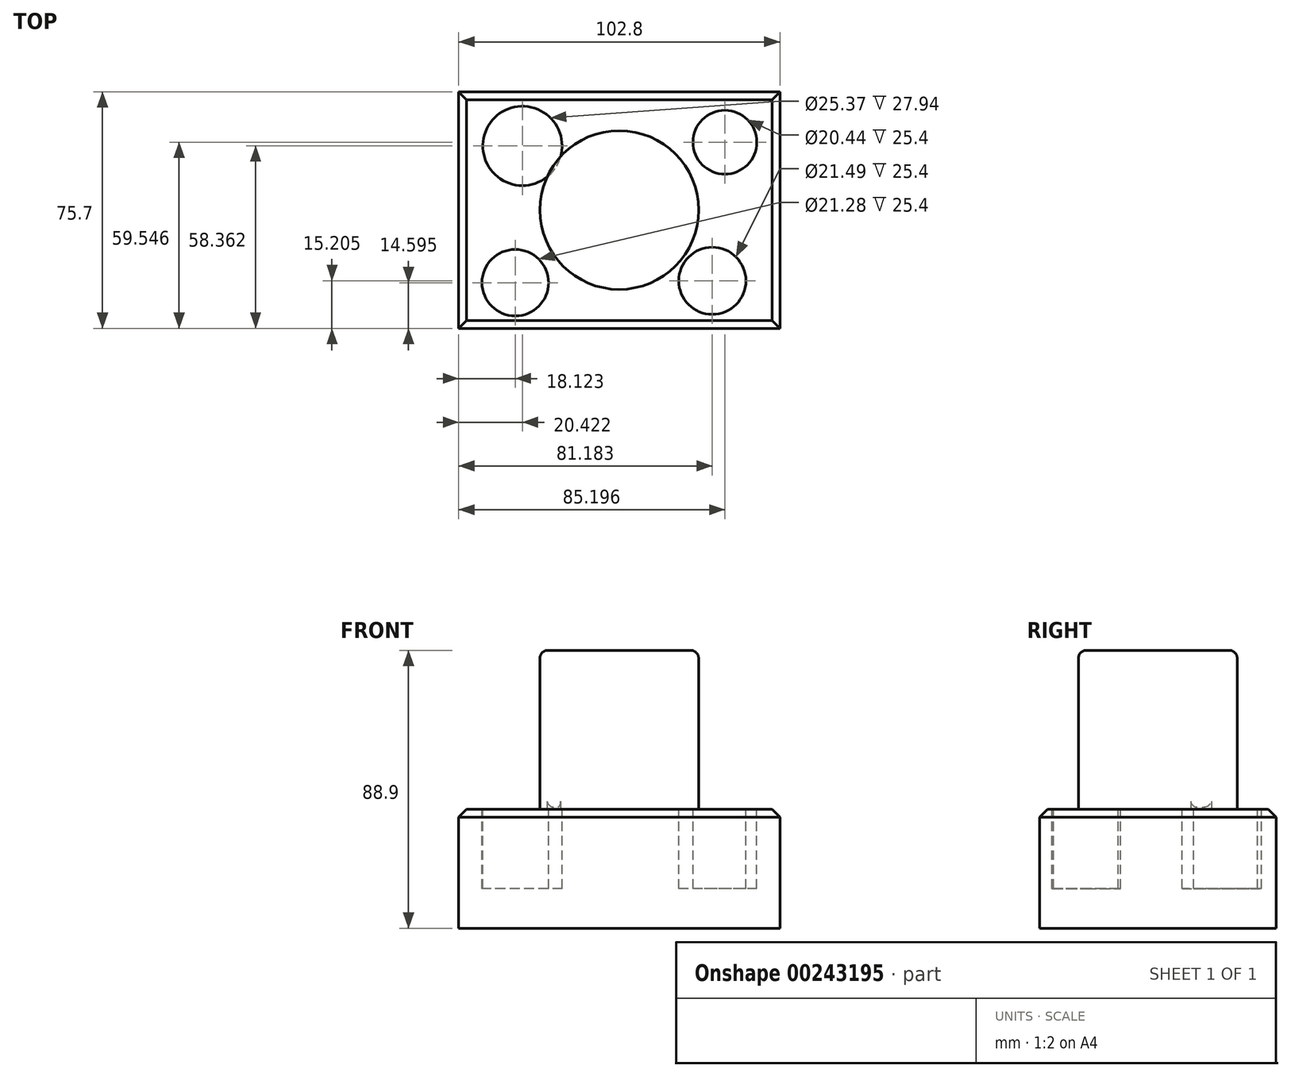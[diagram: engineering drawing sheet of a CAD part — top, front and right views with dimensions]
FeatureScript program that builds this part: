
annotation { "Feature Type Name" : "Feature", "Feature Type Description" : "" }
export const myFeature = defineFeature(function(context is Context, id is Id, definition is map)
    precondition{}
    {
        {
            var Q0;
            Q0=qCreatedBy(makeId("Top.planeOp"),FACE);
            var sketch = newSketch(context, id + "F0", { "sketchPlane" : qUnion([Q0])});
            skLineSegment(sketch, "E0.bottom", {"start": v(-51.4, 37.85) * mm, "end": v(51.4, 37.85) * mm});
            skLineSegment(sketch, "E0.top", {"start": v(-51.4, -37.85) * mm, "end": v(51.4, -37.85) * mm});
            skLineSegment(sketch, "E0.left", {"start": v(-51.4, 37.85) * mm, "end": v(-51.4, -37.85) * mm});
            skLineSegment(sketch, "E0.right", {"start": v(51.4, 37.85) * mm, "end": v(51.4, -37.85) * mm});
            skPoint(sketch, "E0.middle", {"position": v(0, 0) * mm});
            skSolve(sketch);
        }
        {
            var Q0;
            Q0=makeQuery(id+"F0.imprint","IMPRINT",FACE,{"disambiguationData":[TD([[makeQuery(id+"F0.imprint","IMPRINT",EDGE,{"derivedFrom":sQuery(id+"F0.wireOp",EDGE,"E0.bottom")}),-1.0]])]});
            extrude(context, id + "F1", {"entities" : qUnion([Q0]), "depth" : 38.1 * mm});
        }
        {
            var Q0;
            Q0=makeQuery(id+"F1.opExtrude","CAP_FACE",FACE,{"disambiguationData":[OSD([sQuery(id+"F0.wireOp",EDGE,"E0.bottom"),sQuery(id+"F0.wireOp",EDGE,"E0.top"),sQuery(id+"F0.wireOp",EDGE,"E0.left"),sQuery(id+"F0.wireOp",EDGE,"E0.right")])],"isStart":false});
            var sketch = newSketch(context, id + "F2", { "sketchPlane" : qUnion([Q0])});
            skLineSegment(sketch, "E1.0.1", {"start": v(-51.4, -37.85) * mm, "end": v(51.4, -37.85) * mm});
            skLineSegment(sketch, "E1.0.3", {"start": v(51.4, 37.85) * mm, "end": v(-51.4, 37.85) * mm});
            skCircle(sketch, "E2", {"center": v(-30.98, 20.51) * mm, "radius": 12.68 * mm});
            skPoint(sketch, "E2.first.point", {"position": v(-38.59, 10.36) * mm});
            skPoint(sketch, "E2.second.point", {"position": v(-21.36, 28.78) * mm});
            skPoint(sketch, "E2.third.point", {"position": v(-23.1, 10.57) * mm});
            skCircle(sketch, "E3", {"center": v(33.8, 21.7) * mm, "radius": 10.22 * mm});
            skPoint(sketch, "E3.first.point", {"position": v(39.42, 30.23) * mm});
            skPoint(sketch, "E3.second.point", {"position": v(23.63, 20.64) * mm});
            skPoint(sketch, "E3.third.point", {"position": v(41.09, 14.54) * mm});
            skCircle(sketch, "E4", {"center": v(-33.28, -23.25) * mm, "radius": 10.64 * mm});
            skCircle(sketch, "E5", {"center": v(29.78, -22.64) * mm, "radius": 10.74 * mm});
            skSolve(sketch);
        }
        {
            var Q0;
            Q0=makeQuery(id+"F2.imprint","IMPRINT",FACE,{"disambiguationData":[TD([[makeQuery(id+"F2.imprint","IMPRINT",EDGE,{"derivedFrom":sQuery(id+"F2.wireOp",EDGE,"E2")}),1.0]])]});
            var Q1;
            Q1=makeQuery(id+"F2.imprint","IMPRINT",FACE,{"disambiguationData":[TD([[makeQuery(id+"F2.imprint","IMPRINT",EDGE,{"derivedFrom":sQuery(id+"F2.wireOp",EDGE,"E3")}),1.0]])]});
            var Q2;
            Q2=makeQuery(id+"F2.imprint","IMPRINT",FACE,{"disambiguationData":[TD([[makeQuery(id+"F2.imprint","IMPRINT",EDGE,{"derivedFrom":sQuery(id+"F2.wireOp",EDGE,"E5")}),1.0]])]});
            var Q3;
            Q3=makeQuery(id+"F2.imprint","IMPRINT",FACE,{"disambiguationData":[TD([[makeQuery(id+"F2.imprint","IMPRINT",EDGE,{"derivedFrom":sQuery(id+"F2.wireOp",EDGE,"E4")}),1.0]])]});
            extrude(context, id + "F3", {"entities" : qUnion([Q0, Q1, Q2, Q3]), "operationType" : NewBodyOperationType.REMOVE, "oppositeDirection" : true, "depth" : 25.4 * mm});
        }
        {
            var Q0;
            Q0=qCreatedBy(makeId("Front.planeOp"),FACE);
            var sketch = newSketch(context, id + "F4", { "sketchPlane" : qUnion([Q0])});
            skLineSegment(sketch, "E6.bottom", {"start": v(0, 38.1) * mm, "end": v(-25.4, 38.1) * mm});
            skLineSegment(sketch, "E6.top", {"start": v(0, 88.9) * mm, "end": v(-25.4, 88.9) * mm});
            skLineSegment(sketch, "E6.left", {"start": v(0, 38.1) * mm, "end": v(0, 88.9) * mm});
            skLineSegment(sketch, "E6.right", {"start": v(-25.4, 38.1) * mm, "end": v(-25.4, 88.9) * mm});
            skLineSegment(sketch, "E7.left", {"start": v(-25.4, 38.1) * mm, "end": v(-25.4, 38.1) * mm});
            skSolve(sketch);
        }
        {
            var Q0;
            Q0=makeQuery(id+"F4.imprint","IMPRINT",FACE,{"disambiguationData":[TD([[makeQuery(id+"F4.imprint","IMPRINT",EDGE,{"derivedFrom":sQuery(id+"F4.wireOp",EDGE,"E6.bottom")}),-1.0]])]});
            var Q1;
            Q1=sQuery(id+"F4.wireOp",EDGE,"E6.left");
            revolve(context, id + "F5", {"operationType" : NewBodyOperationType.ADD, "entities" : qUnion([Q0]), "axis" : qUnion([Q1]), "revolveType" : RevolveType.FULL});
        }
        {
            var Q0;
            Q0=makeQuery(id+"F1.opExtrude","SWEPT_FACE",FACE,{"disambiguationData":[OSD([sQuery(id+"F0.wireOp",EDGE,"E0.left")])]});
            var sketch = newSketch(context, id + "F6", { "sketchPlane" : qUnion([Q0])});
            skLineSegment(sketch, "E8.bottom", {"start": v(3.39, 70.39) * mm, "end": v(22.7, 70.39) * mm});
            skLineSegment(sketch, "E8.top", {"start": v(3.39, 51.41) * mm, "end": v(22.7, 51.41) * mm});
            skLineSegment(sketch, "E8.left", {"start": v(3.39, 70.39) * mm, "end": v(3.39, 51.41) * mm});
            skLineSegment(sketch, "E8.right", {"start": v(22.7, 70.39) * mm, "end": v(22.7, 51.41) * mm});
            skSolve(sketch);
        }
        {
            var Q0;
            Q0=makeQuery(id+"F6.imprint","IMPRINT",FACE,{"disambiguationData":[TD([[makeQuery(id+"F6.imprint","IMPRINT",EDGE,{"derivedFrom":sQuery(id+"F6.wireOp",EDGE,"E8.bottom")}),-1.0]])]});
            var Q1;
            Q1=makeQuery(id+"F5.opRevolve","SWEPT_FACE",FACE,{"disambiguationData":[OSD([sQuery(id+"F4.wireOp",EDGE,"E6.right")])]});
            revolve(context, id + "F7", {"operationType" : NewBodyOperationType.REMOVE, "entities" : qUnion([Q0]), "axis" : qUnion([Q1]), "revolveType" : RevolveType.FULL, "oppositeDirection" : true});
        }
        {
            var Q0;
            {var subQ0=sQuery(id+"F4.wireOp",EDGE,"E6.bottom");var subQ1=sQuery(id+"F0.wireOp",EDGE,"E0.top");var subQ2=sQuery(id+"F4.wireOp",EDGE,"E6.right");Q0=makeQuery(id+"F5.boolean.opBoolean","SPLIT",EDGE,{"disambiguationData":[TD([makeQuery(id+"F1.opExtrude","CAP_FACE",FACE,{"disambiguationData":[OSD([sQuery(id+"F0.wireOp",EDGE,"E0.bottom"),subQ1,sQuery(id+"F0.wireOp",EDGE,"E0.left"),sQuery(id+"F0.wireOp",EDGE,"E0.right")])],"isStart":false}),makeQuery(id+"F1.opExtrude","SWEPT_FACE",FACE,{"disambiguationData":[OSD([subQ1])]}),makeQuery(id+"F3.boolean.opBoolean","COPY",FACE,{"derivedFrom":makeQuery(id+"F3.opExtrude","SWEPT_FACE",FACE,{"disambiguationData":[OSD([sQuery(id+"F2.wireOp",EDGE,"E5")])]})}),makeQuery(id+"F5.opRevolve","SWEPT_FACE",FACE,{"disambiguationData":[OSD([subQ0])]}),makeQuery(id+"F5.opRevolve","SWEPT_FACE",FACE,{"disambiguationData":[OSD([subQ2])]})]),OD(0.0)],"derivedFrom":makeQuery(id+"F5.opRevolve","SWEPT_EDGE",EDGE,{"disambiguationData":[OSD([subQ1,subQ0,subQ2])]})});}
            var Q1;
            Q1=makeQuery(id+"F5.opRevolve","SWEPT_FACE",FACE,{"disambiguationData":[OSD([sQuery(id+"F4.wireOp",EDGE,"E6.top")])]});
            fillet(context, id + "F8", {"entities" : qUnion([Q0, Q1]), "radius" : 2.54 * mm, "tangentPropagation" : true, "allowEdgeOverflow" : false});
        }
        {
            var Q0;
            Q0=makeQuery(id+"F1.opExtrude","CAP_EDGE",EDGE,{"disambiguationData":[OSD([sQuery(id+"F0.wireOp",EDGE,"E0.left")])],"isStart":false});
            var Q1;
            Q1=makeQuery(id+"F1.opExtrude","CAP_EDGE",EDGE,{"disambiguationData":[OSD([sQuery(id+"F0.wireOp",EDGE,"E0.bottom")])],"isStart":false});
            var Q2;
            Q2=makeQuery(id+"F1.opExtrude","CAP_EDGE",EDGE,{"disambiguationData":[OSD([sQuery(id+"F0.wireOp",EDGE,"E0.right")])],"isStart":false});
            var Q3;
            {var subQ0=sQuery(id+"F0.wireOp",EDGE,"E0.left");var subQ1=sQuery(id+"F0.wireOp",EDGE,"E0.top");Q3=makeQuery(id+"F5.boolean.opBoolean","SPLIT",EDGE,{"disambiguationData":[TD([makeQuery(id+"F1.opExtrude","CAP_FACE",FACE,{"disambiguationData":[OSD([sQuery(id+"F0.wireOp",EDGE,"E0.bottom"),subQ1,subQ0,sQuery(id+"F0.wireOp",EDGE,"E0.right")])],"isStart":false}),makeQuery(id+"F1.opExtrude","SWEPT_FACE",FACE,{"disambiguationData":[OSD([subQ1])]}),makeQuery(id+"F1.opExtrude","SWEPT_FACE",FACE,{"disambiguationData":[OSD([subQ0])]}),makeQuery(id+"F5.opRevolve","SWEPT_FACE",FACE,{"disambiguationData":[OSD([sQuery(id+"F4.wireOp",EDGE,"E6.bottom")])]}),makeQuery(id+"F5.opRevolve","SWEPT_FACE",FACE,{"disambiguationData":[OSD([sQuery(id+"F4.wireOp",EDGE,"E6.right")])]})])],"derivedFrom":makeQuery(id+"F1.opExtrude","CAP_EDGE",EDGE,{"disambiguationData":[OSD([subQ1])],"isStart":false})});}
            chamfer(context, id + "F9", {"entities" : qUnion([Q0, Q1, Q2, Q3]), "width" : 2.54 * mm, "tangentPropagation" : true});
        }
    });
